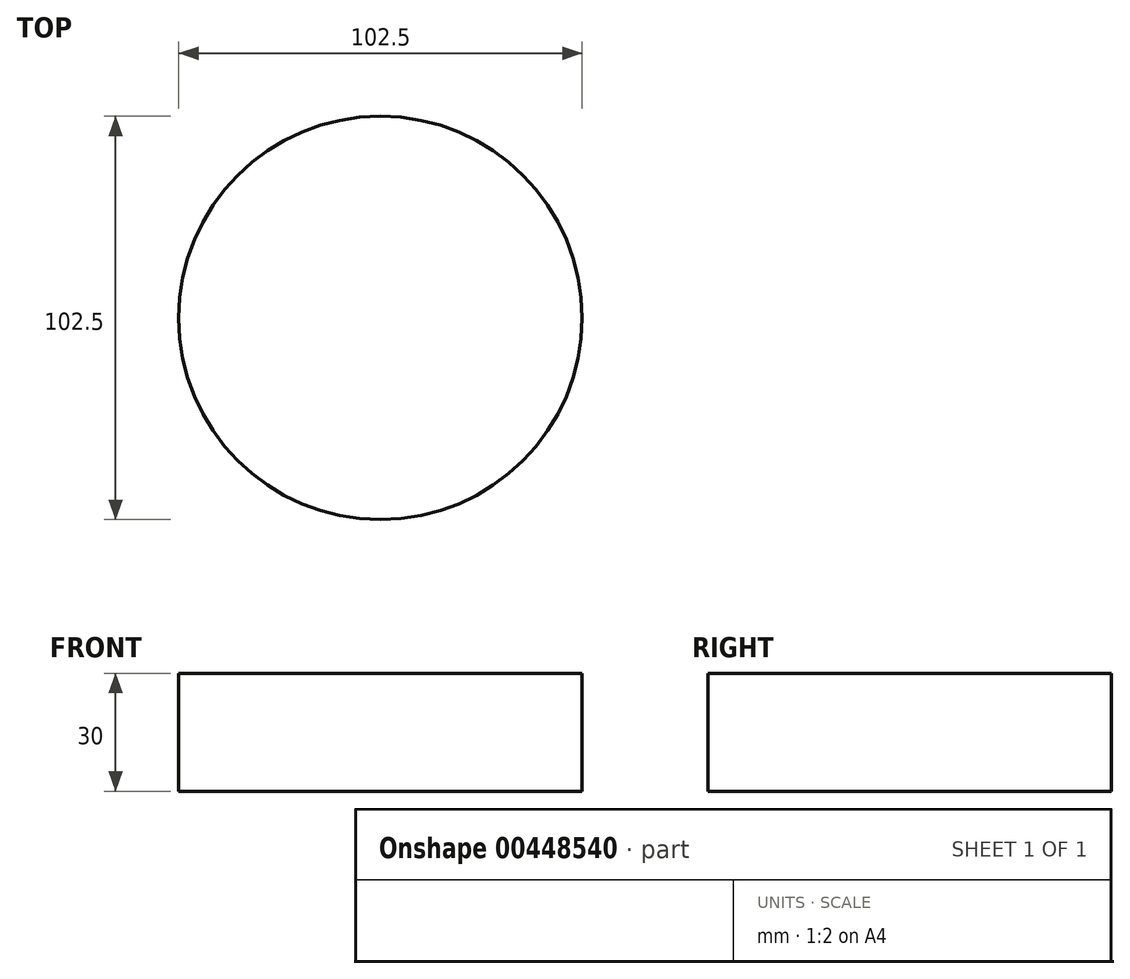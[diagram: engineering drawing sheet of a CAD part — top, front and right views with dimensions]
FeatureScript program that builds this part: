
annotation { "Feature Type Name" : "Feature", "Feature Type Description" : "" }
export const myFeature = defineFeature(function(context is Context, id is Id, definition is map)
    precondition{}
    {
        {
            var Q0;
            Q0=qCreatedBy(makeId("Top.planeOp"),FACE);
            var sketch = newSketch(context, id + "F0", { "sketchPlane" : qUnion([Q0])});
            skCircle(sketch, "E0", {"center": v(0, 0) * mm, "radius": 51.25 * mm});
            skSolve(sketch);
        }
        {
            var Q0;
            Q0 = qSketchRegion(id + "F0", true);
            extrude(context, id + "F1", {"entities" : qUnion([Q0]), "depth" : 30 * mm});
        }
    });
